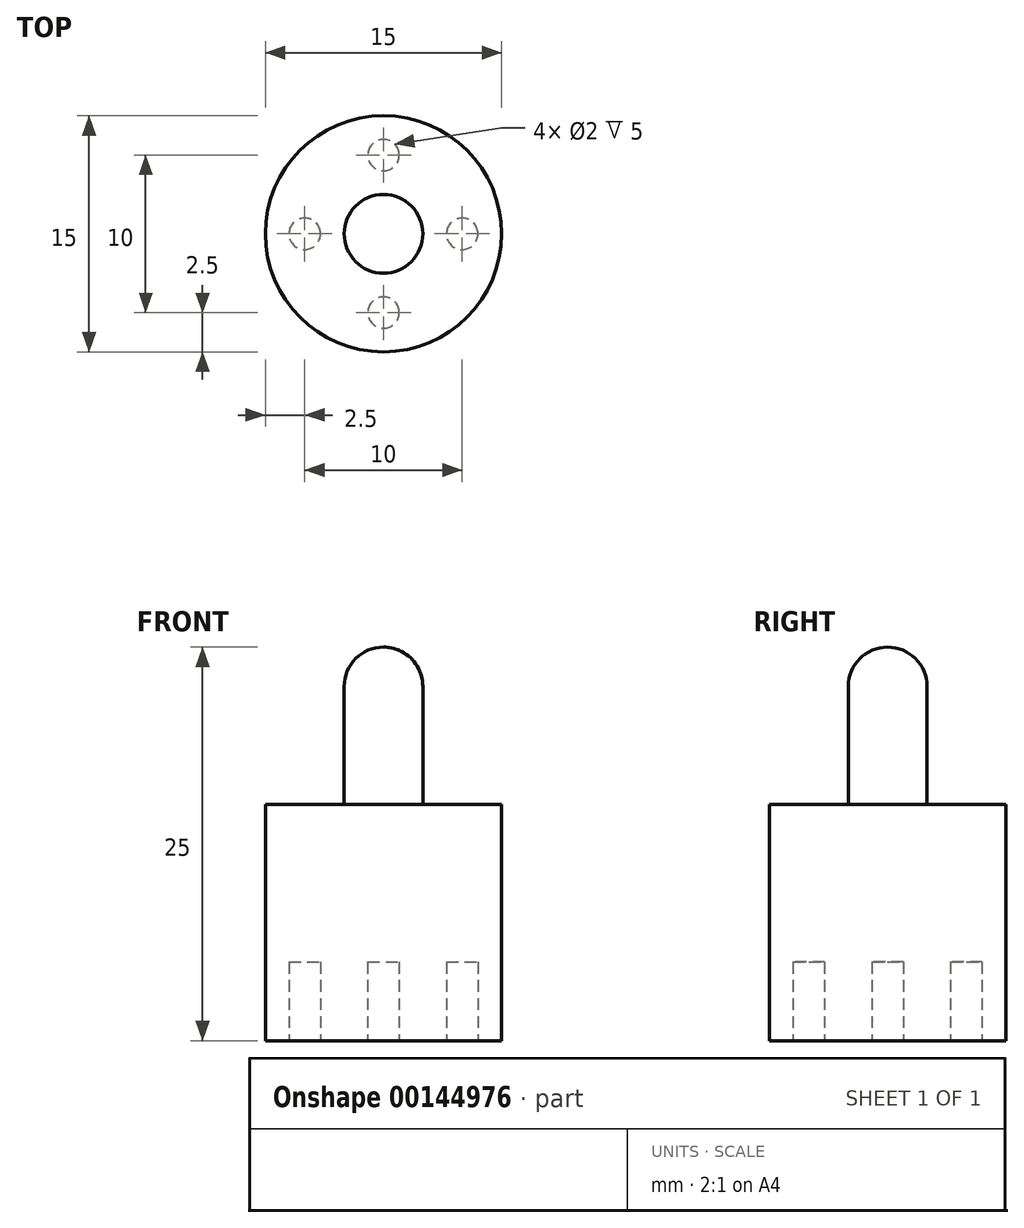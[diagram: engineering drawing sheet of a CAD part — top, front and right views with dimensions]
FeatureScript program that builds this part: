
annotation { "Feature Type Name" : "Feature", "Feature Type Description" : "" }
export const myFeature = defineFeature(function(context is Context, id is Id, definition is map)
    precondition{}
    {
        {
            var Q0;
            Q0=qCreatedBy(makeId("Top.planeOp"),FACE);
            var sketch = newSketch(context, id + "F0", { "sketchPlane" : qUnion([Q0])});
            skCircle(sketch, "E0", {"center": v(0, 0) * mm, "radius": 7.5 * mm});
            skSolve(sketch);
        }
        {
            var Q0;
            Q0 = qSketchRegion(id + "F0", true);
            extrude(context, id + "F1", {"entities" : qUnion([Q0]), "depth" : 15 * mm});
        }
        {
            var Q0;
            Q0=makeQuery(id+"F1.opExtrude","CAP_FACE",FACE,{"disambiguationData":[OSD([sQuery(id+"F0.wireOp",EDGE,"E0")])],"isStart":true});
            var sketch = newSketch(context, id + "F2", { "sketchPlane" : qUnion([Q0])});
            skCircle(sketch, "E1", {"center": v(0, 5) * mm, "radius": 1 * mm});
            skCircle(sketch, "E2", {"center": v(-5, 0) * mm, "radius": 1 * mm});
            skCircle(sketch, "E3", {"center": v(0, -5) * mm, "radius": 1 * mm});
            skCircle(sketch, "E4", {"center": v(5, 0) * mm, "radius": 1 * mm});
            skSolve(sketch);
        }
        {
            var Q0;
            Q0 = qSketchRegion(id + "F2", true);
            extrude(context, id + "F3", {"entities" : qUnion([Q0]), "operationType" : NewBodyOperationType.REMOVE, "oppositeDirection" : true, "depth" : 5 * mm});
        }
        {
            var Q0;
            Q0=makeQuery(id+"F1.opExtrude","CAP_FACE",FACE,{"disambiguationData":[OSD([sQuery(id+"F0.wireOp",EDGE,"E0")])],"isStart":false});
            var sketch = newSketch(context, id + "F4", { "sketchPlane" : qUnion([Q0])});
            skCircle(sketch, "E5", {"center": v(0, 0) * mm, "radius": 2.5 * mm});
            skSolve(sketch);
        }
        {
            var Q0;
            Q0 = qSketchRegion(id + "F4", true);
            extrude(context, id + "F5", {"entities" : qUnion([Q0]), "operationType" : NewBodyOperationType.ADD, "depth" : 10 * mm});
        }
        {
            var Q0;
            Q0=makeQuery(id+"F5.opExtrude","CAP_EDGE",EDGE,{"disambiguationData":[OSD([sQuery(id+"F4.wireOp",EDGE,"E5")])],"isStart":false});
            fillet(context, id + "F6", {"entities" : qUnion([Q0]), "radius" : 2.5 * mm, "tangentPropagation" : true, "allowEdgeOverflow" : false});
        }
    });
